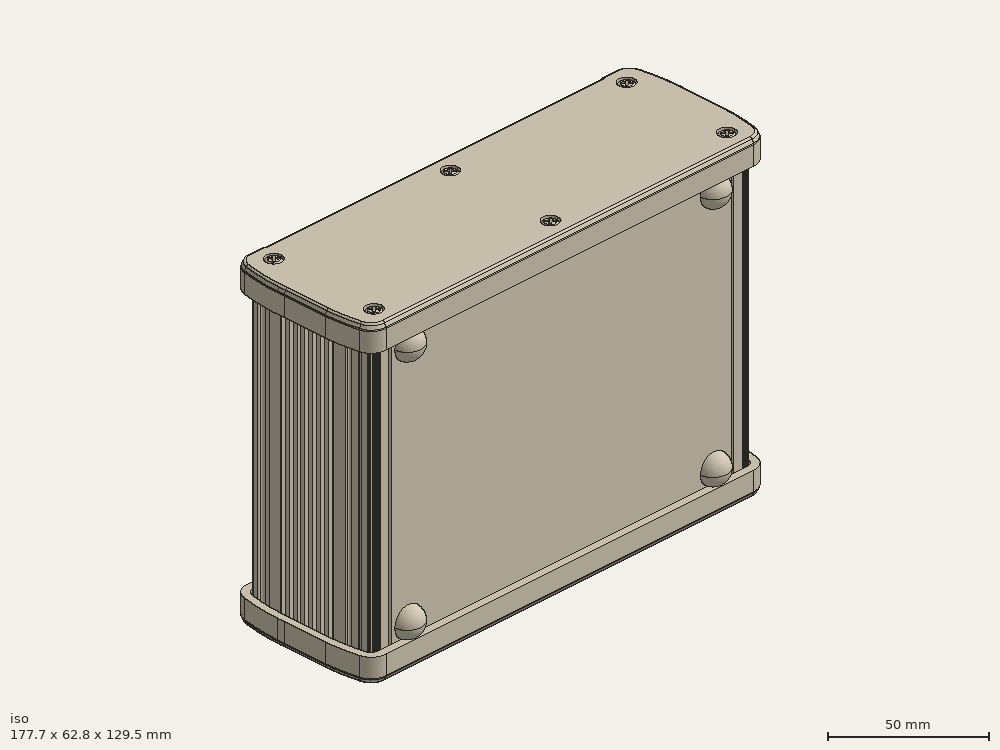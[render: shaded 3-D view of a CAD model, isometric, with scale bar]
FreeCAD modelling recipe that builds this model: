
FCSTD DOCUMENT  (FreeCAD 0.19R24276 (Git))
Label: loraPy04132022
License: All rights reserved
LicenseURL: http://en.wikipedia.org/wiki/All_rights_reserved
objects: Part::Cylinder×12, Part::Box×9, Part::MultiFuse×6, Part::Cut×3, Part::Feature×2
note: 32 computed .brp shape members not serialized (recipe doc carries the construction recipe); baked Part::Feature solids carry a one-line shape summary decoded from their .brp

FEATURE [Part::Box] Box  label="base"
  AttacherType = Attacher::AttachEngine3D
  Height = 100
  Length = 160
  Placement = pos=(0,14.6,4) rot=(0,0,1;0rad)
  Width = 1.6
FEATURE [Part::Feature] Feature  label="EX-64-002"
  Placement = pos=(80,2.7,54) rot=(0,0,1;0rad)
  shape: bbox 178.8 x 63.35 x 129.6 mm, 1628 faces, 33 solids (baked)
FEATURE [Part::Box] Box001  label="base001"
  AttacherType = Attacher::AttachEngine3D
  Height = 100
  Length = 155
  Placement = pos=(2.5,11.7,4) rot=(0,0,1;0rad)
  Width = 2.9
FEATURE [Part::Feature] Feature001  label="Odroid-C1+002"
  Placement = pos=(48,2,72) rot=(-1,0,0;3.14159rad)
  shape: bbox 87.6 x 21.76 x 59.54 mm, 16908 faces, 571 solids (baked)
FEATURE [Part::Box] Box002  label="e5mini"
  AttacherType = Attacher::AttachEngine3D
  Height = 23
  Length = 61
  Width = 6
FEATURE [Part::Cylinder] Cylinder  label="m2s"
  Angle = 360
  AttacherType = Attacher::AttachEngine3D
  Height = 10
  Placement = pos=(14,0,3) rot=(1,0,0;1.5708rad)
  Radius = 1.2
FEATURE [Part::Cylinder] Cylinder001  label="m2s001"
  Angle = 360
  AttacherType = Attacher::AttachEngine3D
  Height = 10
  Placement = pos=(14,0,20) rot=(1,0,0;1.5708rad)
  Radius = 1.2
FEATURE [Part::Cylinder] Cylinder002  label="m2s002"
  Angle = 360
  AttacherType = Attacher::AttachEngine3D
  Height = 10
  Placement = pos=(49,0,20) rot=(1,0,0;1.5708rad)
  Radius = 1.2
FEATURE [Part::Cylinder] Cylinder003  label="m2s003"
  Angle = 360
  AttacherType = Attacher::AttachEngine3D
  Height = 10
  Placement = pos=(49,0,3) rot=(1,0,0;1.5708rad)
  Radius = 1.2
FEATURE [Part::MultiFuse] Fusion  label="e5MiniCuts"
  Placement = pos=(0,6,0) rot=(0,0,1;0rad)
  Shapes = -> [Cylinder,Cylinder001,Cylinder002,Cylinder003]
FEATURE [Part::Cut] Cut  label="e5Mini"
  Base = -> Box002
  Placement = pos=(30,5.7,15) rot=(0,0,1;0rad)
  Tool = -> Fusion
FEATURE [Part::MultiFuse] Fusion001  label="base002"
  Shapes = -> [Box001,Box]
FEATURE [Part::Cylinder] Cylinder004  label="m2s004"
  Angle = 360
  AttacherType = Attacher::AttachEngine3D
  Height = 10
  Placement = pos=(49,0,3) rot=(1,0,0;1.5708rad)
  Radius = 1.6
FEATURE [Part::Cylinder] Cylinder005  label="m2s005"
  Angle = 360
  AttacherType = Attacher::AttachEngine3D
  Height = 10
  Placement = pos=(14,0,20) rot=(1,0,0;1.5708rad)
  Radius = 1.6
FEATURE [Part::Cylinder] Cylinder006  label="m2s006"
  Angle = 360
  AttacherType = Attacher::AttachEngine3D
  Height = 10
  Placement = pos=(14,0,3) rot=(1,0,0;1.5708rad)
  Radius = 1.6
FEATURE [Part::Cylinder] Cylinder007  label="m2s007"
  Angle = 360
  AttacherType = Attacher::AttachEngine3D
  Height = 10
  Placement = pos=(49,0,20) rot=(1,0,0;1.5708rad)
  Radius = 1.6
FEATURE [Part::MultiFuse] Fusion002  label="e5MiniCuts001"
  Placement = pos=(30,16.2,15) rot=(0,0,1;0rad)
  Shapes = -> [Cylinder006,Cylinder005,Cylinder007,Cylinder004]
FEATURE [Part::Cylinder] Cylinder008  label="m2s008"
  Angle = 360
  AttacherType = Attacher::AttachEngine3D
  Height = 10
  Placement = pos=(9,9.9e-15,47.5) rot=(1,0,0;1.5708rad)
  Radius = 2
FEATURE [Part::Cylinder] Cylinder009  label="m2s009"
  Angle = 360
  AttacherType = Attacher::AttachEngine3D
  Height = 10
  Placement = pos=(67,9.9e-15,47.5) rot=(1,0,0;1.5708rad)
  Radius = 2
FEATURE [Part::Cylinder] Cylinder010  label="m2s010"
  Angle = 360
  AttacherType = Attacher::AttachEngine3D
  Height = 10
  Placement = pos=(67,2.08e-14,96.5) rot=(1,0,0;1.5708rad)
  Radius = 2
FEATURE [Part::Cylinder] Cylinder011  label="m2s011"
  Angle = 360
  AttacherType = Attacher::AttachEngine3D
  Height = 10
  Placement = pos=(9,2.08e-14,96.5) rot=(1,0,0;1.5708rad)
  Radius = 2
FEATURE [Part::MultiFuse] Fusion003  label="c1Cuts"
  Placement = pos=(0,16.4,0) rot=(0,0,1;0rad)
  Shapes = -> [Cylinder011,Cylinder008,Cylinder009,Cylinder010]
FEATURE [Part::MultiFuse] Fusion004  label="baseCuts"
  Shapes = -> [Fusion002,Fusion003]
FEATURE [Part::Cut] Cut001  label="base003"
  Base = -> Fusion001
  Tool = -> Fusion004
FEATURE [Part::Box] Box004  label="cuts001"
  AttacherType = Attacher::AttachEngine3D
  Height = 36
  Length = 110
  Placement = pos=(50,10,54) rot=(0,0,1;0rad)
  Width = 10
FEATURE [Part::Box] Box005  label="cuts002"
  AttacherType = Attacher::AttachEngine3D
  Height = 30
  Length = 70
  Placement = pos=(90,10,14.6) rot=(0,0,1;0rad)
  Width = 10
FEATURE [Part::Box] Box006  label="cuts003"
  AttacherType = Attacher::AttachEngine3D
  Height = 25
  Length = 35
  Placement = pos=(0,10,14.6) rot=(0,0,1;0rad)
  Width = 10
FEATURE [Part::Box] Box007  label="cuts004"
  AttacherType = Attacher::AttachEngine3D
  Height = 36
  Length = 35
  Placement = pos=(0,10,54.2) rot=(0,0,1;0rad)
  Width = 10
FEATURE [Part::Box] Box008  label="cuts005"
  AttacherType = Attacher::AttachEngine3D
  Height = 50
  Length = 85
  Placement = pos=(75,10,54) rot=(0,0,1;0rad)
  Width = 10
FEATURE [Part::Box] Box009  label="cuts006"
  AttacherType = Attacher::AttachEngine3D
  Height = 35
  Length = 22
  Placement = pos=(50,10,4) rot=(0,0,1;0rad)
  Width = 10
FEATURE [Part::MultiFuse] Fusion005  label="cuts"
  Shapes = -> [Box004,Box005,Box006,Box007,Box008,Box009]
FEATURE [Part::Cut] Cut002
  Base = -> Cut001
  Tool = -> Fusion005
